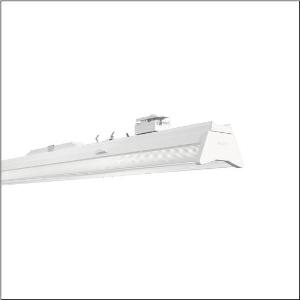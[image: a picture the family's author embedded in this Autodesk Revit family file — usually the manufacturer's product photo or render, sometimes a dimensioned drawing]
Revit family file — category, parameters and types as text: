
# Revit family: licross_21_performance_mo_52td16cn49xg
name_source: partatom
category: Lighting Fixtures
units: mm (PartAtom-declared; Revit-internal decimal feet)

## family parameters
Cut with Voids When Loaded = No
Host = Face
Light Source = No
Part Type = Normal
Room Calculation Point = No
Round Connector Dimension = Use Diameter
Shared = No

## types (1)
- --- (1 x LED, 9240 lm, 50.4 W, 4000K)
    Apparent Load = 50 VA
    CIE Flux Codes = 66 88 96 79 100
    Color Rendering = 80
    Color Temperature = 4000K
    Default Elevation = 1800 mm
    Description = Licross 21 Performance MO, luminaire insert, of sheet steel, galvanised, coil coated, white, length: 1.500mm, width: 120mm, height: 123mm, LED rated luminous flux: 9.240lm, light colour: 840, SDCM (Standard Deviation of Colour Matching)MacAdam ≤ 3 SDCM (initial), control gear: ON/OFF Multilumen, CLOi, with plug, 3-pole, with phase selection, mains connection: 220..240V, AC, 50/60Hz, start of lifetime: 50W, end of service life: 61W, internal wiring halogen-free, primary light control with lens, of plastic, primary optical cover: cover, of PMMA, light emission: direct/indirect distribution, primary light characteristic: symmetric, protection rating (complete): IP54, insulation class (complete): insulation class I (protective earthing), certification: CE, ENEC, UKCA, protection symbol: D if used in an environment with non-conductive dust loads with corresponding accessories, impact resistance: IK06, permissible ambient temperature for indoor applications: -35..+45°C, corresponds to IFS (International Featured Standards) requirements for safety and quality in the food industry, reducing of maximum allowable ambient temperature of 5°C with ceiling mounting, LABS conformity tested according to VDMA 24364:2018-05, The light source and the operating device comply with the requirements of the Ecodesign Regulation (EU) 2019/2020 and are replaceable in accordance with this regulation, packaging unit: 1 piece
    Height = 114 mm
    Lamp = 1 x LED
    Lamp Light Flux = 9240 lm
    Lamp Power = 50.4 W
    Lamp count = 1
    Length = 1500 mm
    Luminous efficacy = 183 lm/W
    Manufacturer = Siteco
    ModVariant = No
    Model = 52TD16CN49XG
    Mounting Place = Ceiling
    Mounting Type = Pendant
    Number of Poles = 1
    OnlyDefault = Yes
    Power Factor = 1
    Product Name = Licross 21 Performance MO
    Product group = luminaire insert | ceiling pendant
    ProductGroupID = 901
    Protection Class = Protection class I
    Protection Degree = IP 54
    RLX_Detail_Level = 1
    RLX_Emergency_Light_Flux = 0 lm
    RLX_Emergency_Type = 0
    RLX_Emergency_Type_DB = No
    RlxData = <blob elided: 32165 chars, md5=87a205c3>
    Socket = socket
    Standby Power = 0 W
    System Light Flux = 9240 lm
    System Power = 50 W
    Type Comments = factory setting: luminous flux: 100 % | (A | C | E) | 117 mA
    Type Image = l_1256138.jpg
    URL = http://relux.com
    VarID = @adj_113069
    Voltage = 0 V
    Weight = 0.00 kg
    Width = 120 mm

## geometry (parser evidence)
native form markers: Blend x4, Sweep x13
no freeform markers — native parametric forms only
